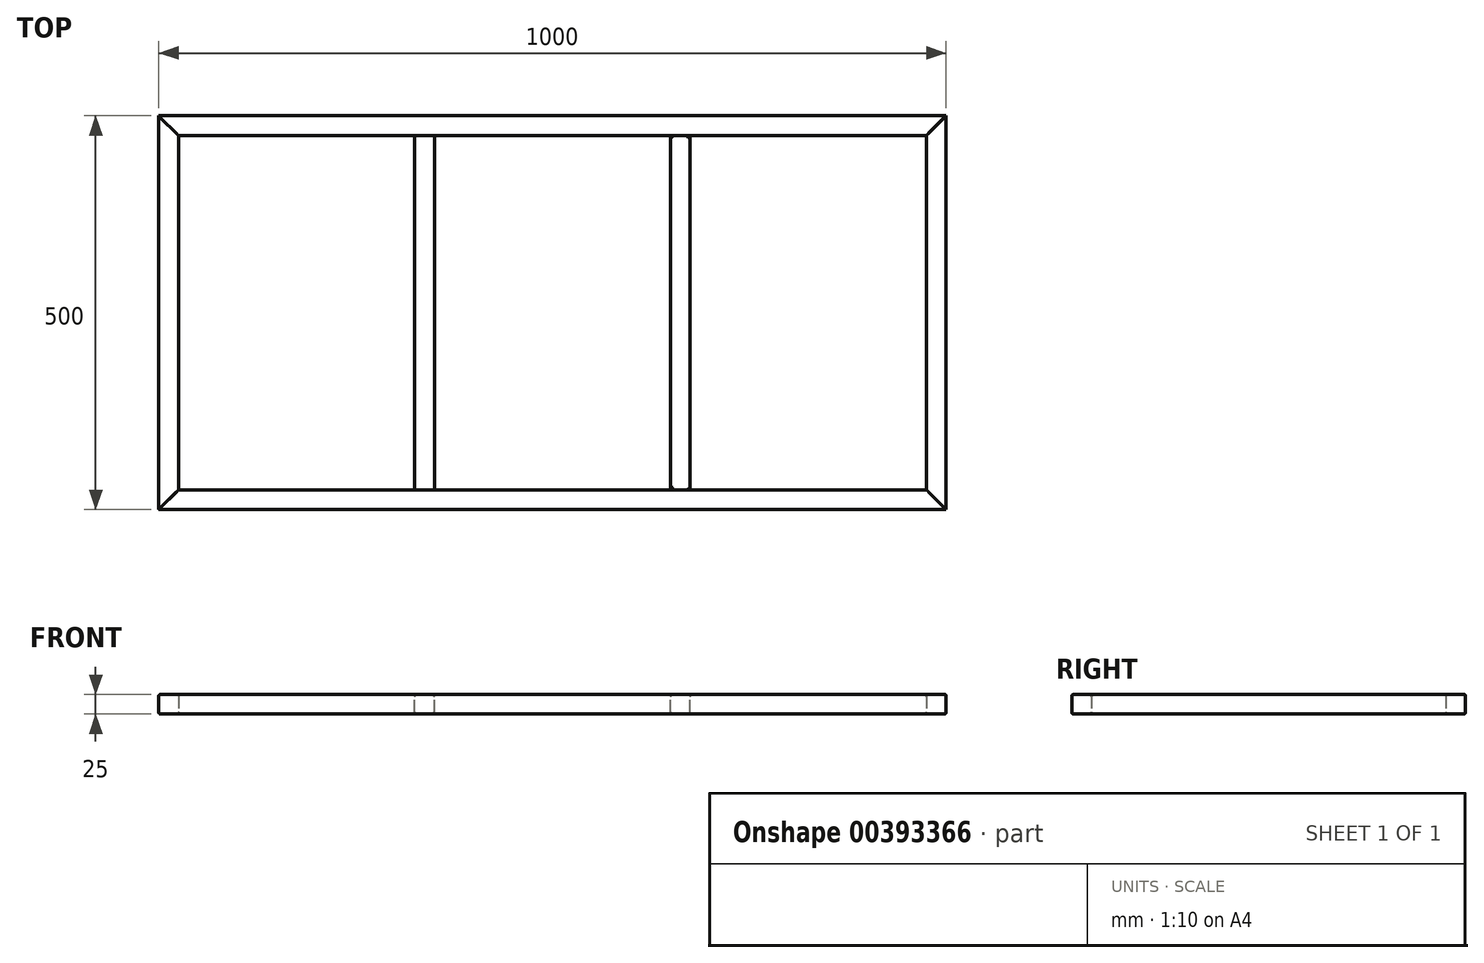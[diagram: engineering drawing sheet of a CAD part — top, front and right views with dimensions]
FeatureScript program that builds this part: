
annotation { "Feature Type Name" : "Feature", "Feature Type Description" : "" }
export const myFeature = defineFeature(function(context is Context, id is Id, definition is map)
    precondition{}
    {
        {
            var Q0;
            Q0=qCreatedBy(makeId("Top.planeOp"),FACE);
            var sketch = newSketch(context, id + "F0", { "sketchPlane" : qUnion([Q0])});
            skLineSegment(sketch, "E0", {"start": v(-558.42, 250) * mm, "end": v(-533.42, 225) * mm});
            skLineSegment(sketch, "E1", {"start": v(-533.42, 225) * mm, "end": v(-533.42, -225) * mm});
            skLineSegment(sketch, "E2", {"start": v(-533.42, -225) * mm, "end": v(-558.42, -250) * mm});
            skLineSegment(sketch, "E3", {"start": v(-558.42, -250) * mm, "end": v(-558.42, 250) * mm});
            skSolve(sketch);
        }
        {
            var Q0;
            Q0 = qSketchRegion(id + "F0", true);
            extrude(context, id + "F1", {"entities" : qUnion([Q0]), "depth" : 25 * mm, "offsetDistance" : 25 * mm});
        }
        {
            var Q0;
            Q0=makeQuery(id+"F1.opExtrude","CAP_EDGE",EDGE,{"disambiguationData":[OSD([sQuery(id+"F0.wireOp",EDGE,"E1")])],"isStart":false});
            var Q1;
            Q1=makeQuery(id+"F1.opExtrude","CAP_EDGE",EDGE,{"disambiguationData":[OSD([sQuery(id+"F0.wireOp",EDGE,"E1")])],"isStart":true});
            var Q2;
            Q2=makeQuery(id+"F1.opExtrude","CAP_EDGE",EDGE,{"disambiguationData":[OSD([sQuery(id+"F0.wireOp",EDGE,"E3")])],"isStart":true});
            var Q3;
            Q3=makeQuery(id+"F1.opExtrude","CAP_EDGE",EDGE,{"disambiguationData":[OSD([sQuery(id+"F0.wireOp",EDGE,"E3")])],"isStart":false});
            fillet(context, id + "F2", {"entities" : qUnion([Q0, Q1, Q2, Q3]), "radius" : 2 * mm, "tangentPropagation" : true, "allowEdgeOverflow" : false});
        }
        {
            var Q0;
            Q0=qCreatedBy(makeId("Top.planeOp"),FACE);
            var sketch = newSketch(context, id + "F3", { "sketchPlane" : qUnion([Q0])});
            skLineSegment(sketch, "E4", {"start": v(-558.42, 250) * mm, "end": v(441.58, 250) * mm});
            skLineSegment(sketch, "E5", {"start": v(441.58, 250) * mm, "end": v(416.58, 225) * mm});
            skLineSegment(sketch, "E6", {"start": v(416.58, 225) * mm, "end": v(-533.42, 225) * mm});
            skLineSegment(sketch, "E7", {"start": v(-533.42, 225) * mm, "end": v(-558.42, 250) * mm});
            skSolve(sketch);
        }
        {
            var Q0;
            Q0 = qSketchRegion(id + "F3", true);
            extrude(context, id + "F4", {"entities" : qUnion([Q0]), "depth" : 25 * mm, "offsetDistance" : 25 * mm});
        }
        {
            var Q0;
            Q0=makeQuery(id+"F4.opExtrude","CAP_EDGE",EDGE,{"disambiguationData":[OSD([sQuery(id+"F3.wireOp",EDGE,"E6")])],"isStart":false});
            var Q1;
            Q1=makeQuery(id+"F4.opExtrude","CAP_EDGE",EDGE,{"disambiguationData":[OSD([sQuery(id+"F3.wireOp",EDGE,"E4")])],"isStart":false});
            var Q2;
            Q2=makeQuery(id+"F4.opExtrude","CAP_EDGE",EDGE,{"disambiguationData":[OSD([sQuery(id+"F3.wireOp",EDGE,"E4")])],"isStart":true});
            var Q3;
            Q3=makeQuery(id+"F4.opExtrude","CAP_EDGE",EDGE,{"disambiguationData":[OSD([sQuery(id+"F3.wireOp",EDGE,"E6")])],"isStart":true});
            fillet(context, id + "F5", {"entities" : qUnion([Q0, Q1, Q2, Q3]), "radius" : 2 * mm, "tangentPropagation" : true, "allowEdgeOverflow" : false});
        }
        {
            var Q0;
            Q0=qCreatedBy(makeId("Top.planeOp"),FACE);
            var sketch = newSketch(context, id + "F6", { "sketchPlane" : qUnion([Q0])});
            skLineSegment(sketch, "E8", {"start": v(-558.42, -250) * mm, "end": v(441.58, -250) * mm});
            skLineSegment(sketch, "E9", {"start": v(416.58, -225) * mm, "end": v(441.58, -250) * mm});
            skLineSegment(sketch, "E10", {"start": v(-558.42, -250) * mm, "end": v(-533.42, -225) * mm});
            skLineSegment(sketch, "E11", {"start": v(-533.42, -225) * mm, "end": v(416.58, -225) * mm});
            skSolve(sketch);
        }
        {
            var Q0;
            Q0 = qSketchRegion(id + "F6", true);
            extrude(context, id + "F7", {"entities" : qUnion([Q0]), "depth" : 25 * mm, "offsetDistance" : 25 * mm});
        }
        {
            var Q0;
            Q0=makeQuery(id+"F7.opExtrude","CAP_EDGE",EDGE,{"disambiguationData":[OSD([sQuery(id+"F6.wireOp",EDGE,"E8")])],"isStart":false});
            var Q1;
            Q1=makeQuery(id+"F7.opExtrude","CAP_EDGE",EDGE,{"disambiguationData":[OSD([sQuery(id+"F6.wireOp",EDGE,"E11")])],"isStart":false});
            var Q2;
            Q2=makeQuery(id+"F7.opExtrude","CAP_EDGE",EDGE,{"disambiguationData":[OSD([sQuery(id+"F6.wireOp",EDGE,"E8")])],"isStart":true});
            var Q3;
            Q3=makeQuery(id+"F7.opExtrude","CAP_EDGE",EDGE,{"disambiguationData":[OSD([sQuery(id+"F6.wireOp",EDGE,"E11")])],"isStart":true});
            fillet(context, id + "F8", {"entities" : qUnion([Q0, Q1, Q2, Q3]), "radius" : 3 * mm, "tangentPropagation" : true, "allowEdgeOverflow" : false});
        }
        {
            var Q0;
            Q0=qCreatedBy(makeId("Top.planeOp"),FACE);
            var sketch = newSketch(context, id + "F9", { "sketchPlane" : qUnion([Q0])});
            skLineSegment(sketch, "E12", {"start": v(441.58, -250) * mm, "end": v(441.58, 250) * mm});
            skLineSegment(sketch, "E13", {"start": v(441.58, 250) * mm, "end": v(416.58, 225) * mm});
            skLineSegment(sketch, "E14", {"start": v(416.58, 225) * mm, "end": v(416.58, -225) * mm});
            skLineSegment(sketch, "E15", {"start": v(416.58, -225) * mm, "end": v(441.58, -250) * mm});
            skSolve(sketch);
        }
        {
            var Q0;
            Q0 = qSketchRegion(id + "F9", true);
            extrude(context, id + "F10", {"entities" : qUnion([Q0]), "depth" : 25 * mm, "offsetDistance" : 25 * mm});
        }
        {
            var Q0;
            Q0=makeQuery(id+"F10.opExtrude","CAP_EDGE",EDGE,{"disambiguationData":[OSD([sQuery(id+"F9.wireOp",EDGE,"E12")])],"isStart":false});
            var Q1;
            Q1=makeQuery(id+"F10.opExtrude","CAP_EDGE",EDGE,{"disambiguationData":[OSD([sQuery(id+"F9.wireOp",EDGE,"E14")])],"isStart":false});
            var Q2;
            Q2=makeQuery(id+"F10.opExtrude","CAP_EDGE",EDGE,{"disambiguationData":[OSD([sQuery(id+"F9.wireOp",EDGE,"E12")])],"isStart":true});
            var Q3;
            Q3=makeQuery(id+"F10.opExtrude","CAP_EDGE",EDGE,{"disambiguationData":[OSD([sQuery(id+"F9.wireOp",EDGE,"E14")])],"isStart":true});
            fillet(context, id + "F11", {"entities" : qUnion([Q0, Q1, Q2, Q3]), "radius" : 3 * mm, "tangentPropagation" : true, "allowEdgeOverflow" : false});
        }
        {
            var Q0;
            Q0=makeQuery(id+"F4.opExtrude","CAP_FACE",FACE,{"disambiguationData":[OSD([sQuery(id+"F3.wireOp",EDGE,"E4"),sQuery(id+"F3.wireOp",EDGE,"E5"),sQuery(id+"F3.wireOp",EDGE,"E6"),sQuery(id+"F3.wireOp",EDGE,"E7")])],"isStart":false});
            var sketch = newSketch(context, id + "F12", { "sketchPlane" : qUnion([Q0])});
            skLineSegment(sketch, "E16.bottom", {"start": v(-233.42, 225) * mm, "end": v(-208.42, 225) * mm});
            skLineSegment(sketch, "E16.top", {"start": v(-233.42, -225) * mm, "end": v(-208.42, -225) * mm});
            skLineSegment(sketch, "E16.left", {"start": v(-233.42, 225) * mm, "end": v(-233.42, -225) * mm});
            skLineSegment(sketch, "E16.right", {"start": v(-208.42, 225) * mm, "end": v(-208.42, -225) * mm});
            skLineSegment(sketch, "E17.bottom", {"start": v(91.58, 225) * mm, "end": v(116.58, 225) * mm});
            skLineSegment(sketch, "E17.top", {"start": v(91.58, -225) * mm, "end": v(116.58, -225) * mm});
            skLineSegment(sketch, "E17.left", {"start": v(91.58, 225) * mm, "end": v(91.58, -225) * mm});
            skLineSegment(sketch, "E17.right", {"start": v(116.58, 225) * mm, "end": v(116.58, -225) * mm});
            skSolve(sketch);
        }
        {
            var Q0;
            Q0 = qSketchRegion(id + "F12", true);
            extrude(context, id + "F13", {"entities" : qUnion([Q0]), "oppositeDirection" : true, "depth" : 25 * mm, "offsetDistance" : 25 * mm});
        }
        {
            var Q0;
            Q0=makeQuery(id+"F13.opExtrude","CAP_EDGE",EDGE,{"disambiguationData":[OSD([sQuery(id+"F12.wireOp",EDGE,"E16.right")])],"isStart":true});
            var Q1;
            Q1=makeQuery(id+"F13.opExtrude","CAP_EDGE",EDGE,{"disambiguationData":[OSD([sQuery(id+"F12.wireOp",EDGE,"E16.left")])],"isStart":true});
            var Q2;
            Q2=makeQuery(id+"F13.opExtrude","CAP_EDGE",EDGE,{"disambiguationData":[OSD([sQuery(id+"F12.wireOp",EDGE,"E16.right")])],"isStart":false});
            var Q3;
            Q3=makeQuery(id+"F13.opExtrude","CAP_FACE",FACE,{"disambiguationData":[OSD([sQuery(id+"F12.wireOp",EDGE,"E17.bottom"),sQuery(id+"F12.wireOp",EDGE,"E17.top"),sQuery(id+"F12.wireOp",EDGE,"E17.left"),sQuery(id+"F12.wireOp",EDGE,"E17.right")])],"isStart":true});
            var Q4;
            Q4=makeQuery(id+"F13.opExtrude","CAP_EDGE",EDGE,{"disambiguationData":[OSD([sQuery(id+"F12.wireOp",EDGE,"E17.right")])],"isStart":true});
            var Q5;
            Q5=makeQuery(id+"F13.opExtrude","CAP_EDGE",EDGE,{"disambiguationData":[OSD([sQuery(id+"F12.wireOp",EDGE,"E17.right")])],"isStart":false});
            var Q6;
            Q6=makeQuery(id+"F13.opExtrude","CAP_EDGE",EDGE,{"disambiguationData":[OSD([sQuery(id+"F12.wireOp",EDGE,"E17.left")])],"isStart":false});
            var Q7;
            Q7=makeQuery(id+"F13.opExtrude","CAP_EDGE",EDGE,{"disambiguationData":[OSD([sQuery(id+"F12.wireOp",EDGE,"E16.left")])],"isStart":false});
            fillet(context, id + "F14", {"entities" : qUnion([Q0, Q1, Q2, Q3, Q4, Q5, Q6, Q7]), "radius" : 3 * mm, "tangentPropagation" : true, "allowEdgeOverflow" : false});
        }
    });
